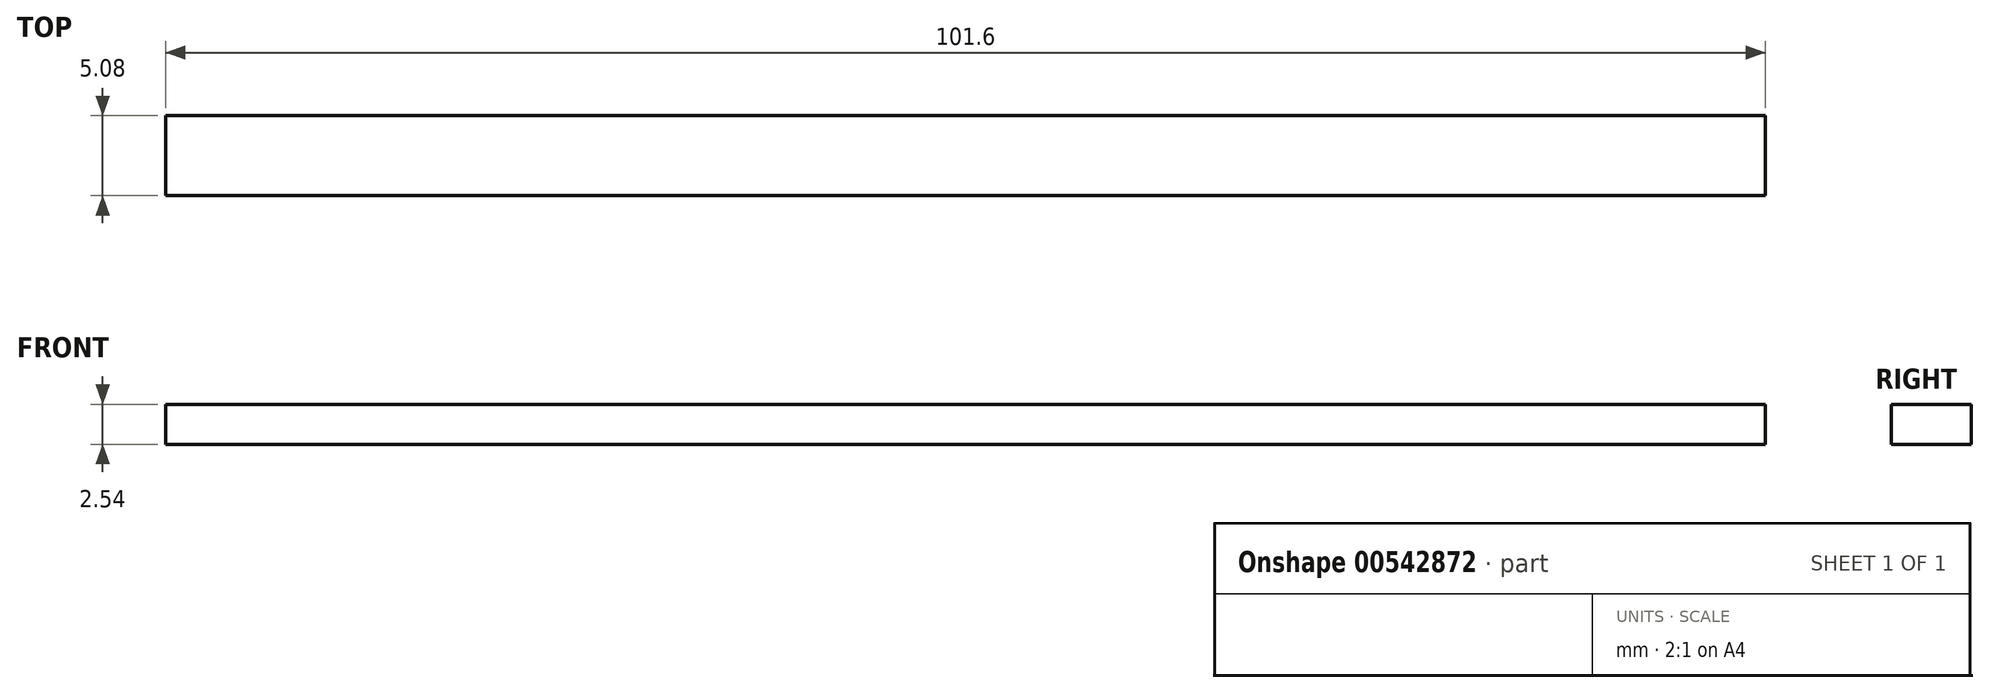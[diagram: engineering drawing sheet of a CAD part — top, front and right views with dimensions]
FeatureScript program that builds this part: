
annotation { "Feature Type Name" : "Feature", "Feature Type Description" : "" }
export const myFeature = defineFeature(function(context is Context, id is Id, definition is map)
    precondition{}
    {
        {
            var Q0;
            Q0=qCreatedBy(makeId("Top.planeOp"),FACE);
            var sketch = newSketch(context, id + "F0", { "sketchPlane" : qUnion([Q0])});
            skLineSegment(sketch, "E0.bottom", {"start": v(0, 0) * mm, "end": v(101.6, 0) * mm});
            skLineSegment(sketch, "E0.top", {"start": v(0, 5.08) * mm, "end": v(101.6, 5.08) * mm});
            skLineSegment(sketch, "E0.left", {"start": v(0, 0) * mm, "end": v(0, 5.08) * mm});
            skLineSegment(sketch, "E0.right", {"start": v(101.6, 0) * mm, "end": v(101.6, 5.08) * mm});
            skSolve(sketch);
        }
        {
            var Q0;
            Q0 = qSketchRegion(id + "F0", true);
            extrude(context, id + "F1", {"entities" : qUnion([Q0]), "depth" : 2.54 * mm, "offsetDistance" : 25.4 * mm});
        }
    });
